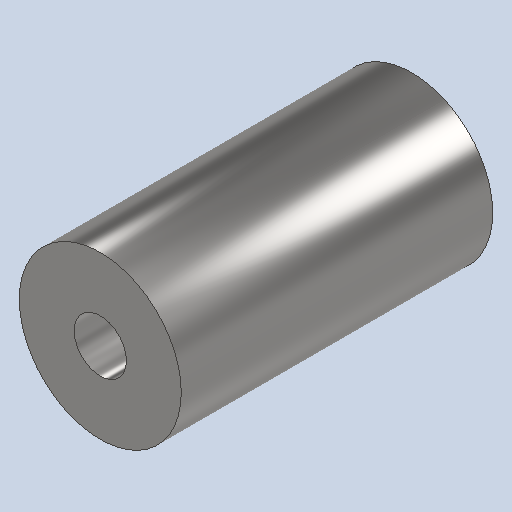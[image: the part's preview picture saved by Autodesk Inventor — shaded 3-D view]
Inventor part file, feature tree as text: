
AUTODESK INVENTOR PART (.ipt)
format: ipt  version: 2022 (Build 260153000, 153)  size: 137,728 bytes
history: native  units: in
note: dims shown in document units (in); Inventor stores cm internally (conversion verified against a paired STEP export)
features: extrude x1
ambient origin geometry x8: Origin, YZ Plane, XZ Plane, XY Plane, X Axis, Y Axis, Z Axis, Center Point
bodies: Solid1 (feature_tree)
feature tree (1):
  extrude  "Extrude1"  [1 undecoded]
note: 1 required parameter value undecoded (feature->parameter linkage not recoverable at this tier; creation-order binding heuristic only, values carry confidence <= 0.55)
